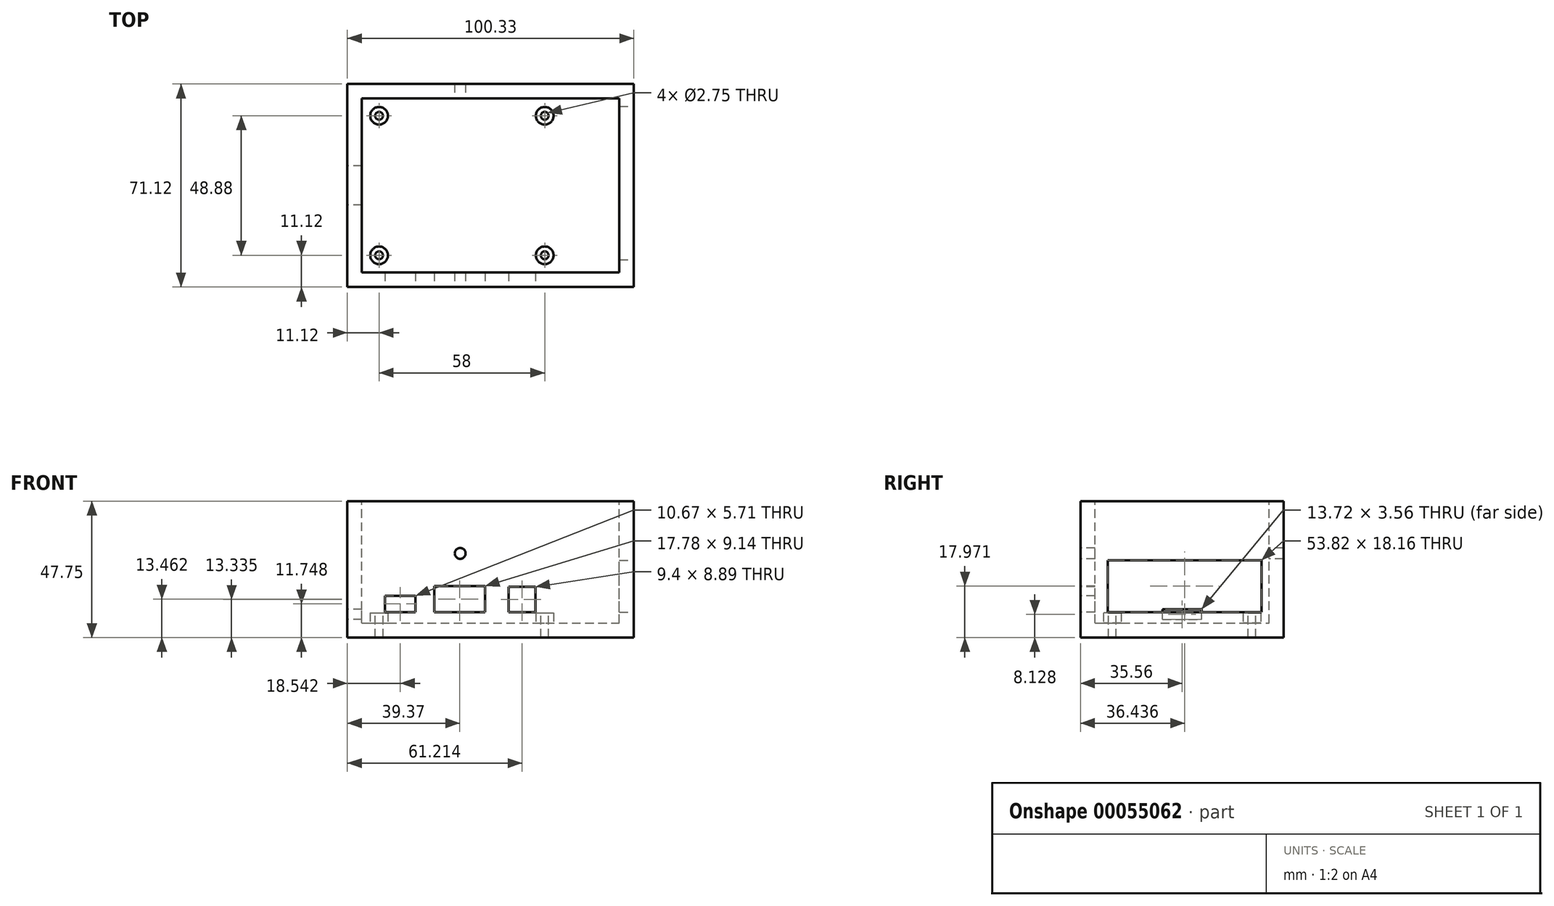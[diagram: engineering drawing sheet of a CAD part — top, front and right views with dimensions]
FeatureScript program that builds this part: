
annotation { "Feature Type Name" : "Feature", "Feature Type Description" : "" }
export const myFeature = defineFeature(function(context is Context, id is Id, definition is map)
    precondition{}
    {
        {
            var Q0;
            Q0=qCreatedBy(makeId("Top.planeOp"),FACE);
            var sketch = newSketch(context, id + "F0", { "sketchPlane" : qUnion([Q0])});
            skLineSegment(sketch, "E0.bottom", {"start": v(0, 0) * mm, "end": v(85.1, 0) * mm, "construction": true});
            skLineSegment(sketch, "E0.top", {"start": v(0, 55.88) * mm, "end": v(85.1, 55.88) * mm, "construction": true});
            skLineSegment(sketch, "E0.left", {"start": v(0, 0) * mm, "end": v(0, 55.88) * mm, "construction": true});
            skLineSegment(sketch, "E0.right", {"start": v(85.1, 0) * mm, "end": v(85.1, 55.88) * mm, "construction": true});
            skLineSegment(sketch, "E1", {"start": v(85.1, 54.61) * mm, "end": v(87.38, 54.61) * mm, "construction": true});
            skLineSegment(sketch, "E2", {"start": v(87.38, 54.61) * mm, "end": v(87.38, 2.29) * mm, "construction": true});
            skLineSegment(sketch, "E3", {"start": v(87.38, 2.29) * mm, "end": v(85.1, 2.29) * mm, "construction": true});
            skLineSegment(sketch, "E4", {"start": v(57.02, 0) * mm, "end": v(57.02, -2.29) * mm, "construction": true});
            skLineSegment(sketch, "E5", {"start": v(57.02, -2.29) * mm, "end": v(50.17, -2.29) * mm, "construction": true});
            skLineSegment(sketch, "E6", {"start": v(50.17, -2.29) * mm, "end": v(50.17, 0) * mm, "construction": true});
            skLineSegment(sketch, "E7", {"start": v(39.37, 0) * mm, "end": v(39.37, -0.76) * mm, "construction": true});
            skLineSegment(sketch, "E8", {"start": v(39.37, -0.76) * mm, "end": v(24.13, -0.76) * mm, "construction": true});
            skLineSegment(sketch, "E9", {"start": v(24.13, -0.76) * mm, "end": v(24.13, 0) * mm, "construction": true});
            skLineSegment(sketch, "E10", {"start": v(14.99, 0) * mm, "end": v(14.99, -1.27) * mm, "construction": true});
            skLineSegment(sketch, "E11", {"start": v(14.99, -1.27) * mm, "end": v(6.86, -1.27) * mm, "construction": true});
            skLineSegment(sketch, "E12", {"start": v(6.86, -1.27) * mm, "end": v(6.86, 0) * mm, "construction": true});
            skLineSegment(sketch, "E13", {"start": v(0, 33.53) * mm, "end": v(-2.54, 33.53) * mm, "construction": true});
            skLineSegment(sketch, "E14", {"start": v(-2.54, 33.53) * mm, "end": v(-2.54, 22.35) * mm, "construction": true});
            skLineSegment(sketch, "E15", {"start": v(-2.54, 22.35) * mm, "end": v(0, 22.35) * mm, "construction": true});
            skCircle(sketch, "E16", {"center": v(3.5, 52.38) * mm, "radius": 1.38 * mm});
            skCircle(sketch, "E17", {"center": v(3.5, 3.5) * mm, "radius": 1.38 * mm});
            skCircle(sketch, "E18", {"center": v(61.5, 3.5) * mm, "radius": 1.38 * mm});
            skCircle(sketch, "E19", {"center": v(61.5, 52.38) * mm, "radius": 1.38 * mm});
            skLineSegment(sketch, "E20.bottom", {"start": v(-2.54, -2.54) * mm, "end": v(87.63, -2.54) * mm});
            skLineSegment(sketch, "E20.top", {"start": v(-2.54, 58.42) * mm, "end": v(87.63, 58.42) * mm});
            skLineSegment(sketch, "E20.left", {"start": v(-2.54, -2.54) * mm, "end": v(-2.54, 58.42) * mm});
            skLineSegment(sketch, "E20.right", {"start": v(87.63, -2.54) * mm, "end": v(87.63, 58.42) * mm});
            skLineSegment(sketch, "E21.0", {"start": v(-7.62, -7.62) * mm, "end": v(92.71, -7.62) * mm});
            skLineSegment(sketch, "E21.1", {"start": v(-7.62, -7.62) * mm, "end": v(-7.62, 63.5) * mm});
            skLineSegment(sketch, "E21.2", {"start": v(-7.62, 63.5) * mm, "end": v(92.71, 63.5) * mm});
            skLineSegment(sketch, "E21.3", {"start": v(92.71, -7.62) * mm, "end": v(92.71, 63.5) * mm});
            skSolve(sketch);
        }
        {
            var Q0;
            Q0=makeQuery(id+"F0.imprint","IMPRINT",FACE,{"disambiguationData":[TD([[makeQuery(id+"F0.imprint","IMPRINT",EDGE,{"derivedFrom":sQuery(id+"F0.wireOp",EDGE,"E20.bottom")}),-1.0]])]});
            extrude(context, id + "F1", {"entities" : qUnion([Q0]), "oppositeDirection" : true, "depth" : 5.08 * mm});
        }
        {
            var Q0;
            Q0=makeQuery(id+"F1.opExtrude","CAP_FACE",FACE,{"disambiguationData":[OSD([sQuery(id+"F0.wireOp",EDGE,"E20.bottom"),sQuery(id+"F0.wireOp",EDGE,"E20.top"),sQuery(id+"F0.wireOp",EDGE,"E20.left"),sQuery(id+"F0.wireOp",EDGE,"E20.right"),sQuery(id+"F0.wireOp",EDGE,"E21.0"),sQuery(id+"F0.wireOp",EDGE,"E21.1"),sQuery(id+"F0.wireOp",EDGE,"E21.2"),sQuery(id+"F0.wireOp",EDGE,"E21.3")])],"isStart":false});
            var sketch = newSketch(context, id + "F2", { "sketchPlane" : qUnion([Q0])});
            skLineSegment(sketch, "E22.bottom", {"start": v(-7.62, 7.62) * mm, "end": v(92.71, 7.62) * mm});
            skLineSegment(sketch, "E22.top", {"start": v(-7.62, -63.5) * mm, "end": v(92.71, -63.5) * mm});
            skLineSegment(sketch, "E22.left", {"start": v(-7.62, 7.62) * mm, "end": v(-7.62, -63.5) * mm});
            skLineSegment(sketch, "E22.right", {"start": v(92.71, 7.62) * mm, "end": v(92.71, -63.5) * mm});
            skSolve(sketch);
        }
        {
            var Q0;
            Q0 = qSketchRegion(id + "F2", true);
            extrude(context, id + "F3", {"entities" : qUnion([Q0]), "operationType" : NewBodyOperationType.ADD, "depth" : 5.08 * mm});
        }
        {
            var Q0;
            Q0=makeQuery(id+"F0.imprint","IMPRINT",FACE,{"disambiguationData":[TD([[makeQuery(id+"F0.imprint","IMPRINT",EDGE,{"derivedFrom":sQuery(id+"F0.wireOp",EDGE,"E16")}),1.0]])]});
            var Q1;
            Q1=makeQuery(id+"F0.imprint","IMPRINT",FACE,{"disambiguationData":[TD([[makeQuery(id+"F0.imprint","IMPRINT",EDGE,{"derivedFrom":sQuery(id+"F0.wireOp",EDGE,"E19")}),1.0]])]});
            var Q2;
            Q2=makeQuery(id+"F0.imprint","IMPRINT",FACE,{"disambiguationData":[TD([[makeQuery(id+"F0.imprint","IMPRINT",EDGE,{"derivedFrom":sQuery(id+"F0.wireOp",EDGE,"E18")}),1.0]])]});
            var Q3;
            Q3=makeQuery(id+"F0.imprint","IMPRINT",FACE,{"disambiguationData":[TD([[makeQuery(id+"F0.imprint","IMPRINT",EDGE,{"derivedFrom":sQuery(id+"F0.wireOp",EDGE,"E17")}),1.0]])]});
            extrude(context, id + "F4", {"entities" : qUnion([Q0, Q1, Q2, Q3]), "operationType" : NewBodyOperationType.REMOVE, "oppositeDirection" : true, "depth" : 25.4 * mm});
        }
        {
            var Q0;
            Q0=makeQuery(id+"F3.opExtrude","CAP_FACE",FACE,{"disambiguationData":[OSD([sQuery(id+"F2.wireOp",EDGE,"E22.bottom"),sQuery(id+"F2.wireOp",EDGE,"E22.top"),sQuery(id+"F2.wireOp",EDGE,"E22.left"),sQuery(id+"F2.wireOp",EDGE,"E22.right")])],"isStart":true});
            var sketch = newSketch(context, id + "F5", { "sketchPlane" : qUnion([Q0])});
            skCircle(sketch, "E23", {"center": v(3.5, 52.38) * mm, "radius": 3.1 * mm});
            skCircle(sketch, "E24", {"center": v(61.5, 52.38) * mm, "radius": 3.1 * mm});
            skCircle(sketch, "E25", {"center": v(61.5, 3.5) * mm, "radius": 3.1 * mm});
            skCircle(sketch, "E26", {"center": v(3.5, 3.5) * mm, "radius": 3.1 * mm});
            skCircle(sketch, "E27", {"center": v(3.5, 52.38) * mm, "radius": 1.38 * mm});
            skCircle(sketch, "E28", {"center": v(3.5, 3.5) * mm, "radius": 1.38 * mm});
            skCircle(sketch, "E29", {"center": v(61.5, 3.5) * mm, "radius": 1.38 * mm});
            skCircle(sketch, "E30", {"center": v(61.5, 52.38) * mm, "radius": 1.38 * mm});
            skSolve(sketch);
        }
        {
            var Q0;
            Q0 = qSketchRegion(id + "F5", true);
            extrude(context, id + "F6", {"entities" : qUnion([Q0]), "operationType" : NewBodyOperationType.ADD, "depth" : 3.56 * mm});
        }
        {
            var Q0;
            Q0=makeQuery(id+"F0.imprint","IMPRINT",FACE,{"disambiguationData":[TD([[makeQuery(id+"F0.imprint","IMPRINT",EDGE,{"derivedFrom":sQuery(id+"F0.wireOp",EDGE,"E20.bottom")}),-1.0]])]});
            extrude(context, id + "F7", {"entities" : qUnion([Q0]), "operationType" : NewBodyOperationType.ADD, "depth" : 37.6 * mm});
        }
        {
            var Q0;
            {var subQ0=sQuery(id+"F0.wireOp",EDGE,"E21.1");Q0=makeQuery(id+"F7.boolean.opBoolean","MERGE",FACE,{"derivedFrom":[makeQuery(id+"F3.boolean.opBoolean","MERGE",FACE,{"derivedFrom":[makeQuery(id+"F1.opExtrude","SWEPT_FACE",FACE,{"disambiguationData":[OSD([subQ0])]}),makeQuery(id+"F3.opExtrude","SWEPT_FACE",FACE,{"disambiguationData":[OSD([sQuery(id+"F2.wireOp",EDGE,"E22.left")])]})]}),makeQuery(id+"F7.opExtrude","SWEPT_FACE",FACE,{"disambiguationData":[OSD([subQ0])]})]});}
            var sketch = newSketch(context, id + "F8", { "sketchPlane" : qUnion([Q0])});
            skLineSegment(sketch, "E31.rect.bottom", {"start": v(-21.08, -3.81) * mm, "end": v(-34.8, -3.81) * mm});
            skLineSegment(sketch, "E31.rect.top", {"start": v(-21.08, -0.25) * mm, "end": v(-34.8, -0.25) * mm});
            skLineSegment(sketch, "E31.rect.left", {"start": v(-21.08, -3.8) * mm, "end": v(-21.08, -0.25) * mm});
            skLineSegment(sketch, "E31.rect.right", {"start": v(-34.8, -3.81) * mm, "end": v(-34.8, -0.25) * mm});
            skPoint(sketch, "E31.rect.middle", {"position": v(-27.94, -2.03) * mm});
            skLineSegment(sketch, "E32.bottom", {"start": v(-33.53, -1.52) * mm, "end": v(-22.35, -1.52) * mm, "construction": true});
            skLineSegment(sketch, "E32.top", {"start": v(-33.53, -2.54) * mm, "end": v(-22.35, -2.54) * mm, "construction": true});
            skLineSegment(sketch, "E32.left", {"start": v(-33.53, -1.52) * mm, "end": v(-33.53, -2.54) * mm, "construction": true});
            skLineSegment(sketch, "E32.right", {"start": v(-22.35, -1.52) * mm, "end": v(-22.35, -2.54) * mm, "construction": true});
            skSolve(sketch);
        }
        {
            var Q0;
            Q0 = qSketchRegion(id + "F8", true);
            extrude(context, id + "F9", {"entities" : qUnion([Q0]), "operationType" : NewBodyOperationType.REMOVE, "endBound" : BoundingType.UP_TO_NEXT, "oppositeDirection" : true, "depth" : 25.4 * mm});
        }
        {
            var Q0;
            {var subQ0=sQuery(id+"F0.wireOp",EDGE,"E21.0");Q0=makeQuery(id+"F7.boolean.opBoolean","MERGE",FACE,{"derivedFrom":[makeQuery(id+"F3.boolean.opBoolean","MERGE",FACE,{"derivedFrom":[makeQuery(id+"F1.opExtrude","SWEPT_FACE",FACE,{"disambiguationData":[OSD([subQ0])]}),makeQuery(id+"F3.opExtrude","SWEPT_FACE",FACE,{"disambiguationData":[OSD([sQuery(id+"F2.wireOp",EDGE,"E22.bottom")])]})]}),makeQuery(id+"F7.opExtrude","SWEPT_FACE",FACE,{"disambiguationData":[OSD([subQ0])]})]});}
            var sketch = newSketch(context, id + "F10", { "sketchPlane" : qUnion([Q0])});
            skLineSegment(sketch, "E33.bottom", {"start": v(6.86, 3.18) * mm, "end": v(14.99, 3.18) * mm, "construction": true});
            skLineSegment(sketch, "E33.top", {"start": v(6.86, 0) * mm, "end": v(14.99, 0) * mm, "construction": true});
            skLineSegment(sketch, "E33.left", {"start": v(6.86, 3.18) * mm, "end": v(6.86, 0) * mm, "construction": true});
            skLineSegment(sketch, "E33.right", {"start": v(14.99, 3.18) * mm, "end": v(14.99, 0) * mm, "construction": true});
            skLineSegment(sketch, "E34.bottom", {"start": v(24.13, 6.6) * mm, "end": v(39.37, 6.6) * mm, "construction": true});
            skLineSegment(sketch, "E34.top", {"start": v(24.13, 0) * mm, "end": v(39.37, 0) * mm, "construction": true});
            skLineSegment(sketch, "E34.left", {"start": v(24.13, 6.6) * mm, "end": v(24.13, 0) * mm, "construction": true});
            skLineSegment(sketch, "E34.right", {"start": v(39.37, 6.6) * mm, "end": v(39.37, 0) * mm, "construction": true});
            skLineSegment(sketch, "E35.bottom", {"start": v(50.17, 6.35) * mm, "end": v(57.02, 6.35) * mm, "construction": true});
            skLineSegment(sketch, "E35.top", {"start": v(50.17, 0) * mm, "end": v(57.02, 0) * mm, "construction": true});
            skLineSegment(sketch, "E35.left", {"start": v(50.17, 6.35) * mm, "end": v(50.17, 0) * mm, "construction": true});
            skLineSegment(sketch, "E35.right", {"start": v(57.02, 6.35) * mm, "end": v(57.02, 0) * mm, "construction": true});
            skLineSegment(sketch, "E36.bottom", {"start": v(16.26, 4.45) * mm, "end": v(5.59, 4.45) * mm});
            skLineSegment(sketch, "E36.top", {"start": v(16.26, -1.27) * mm, "end": v(5.59, -1.27) * mm});
            skLineSegment(sketch, "E36.left", {"start": v(16.26, 4.45) * mm, "end": v(16.26, -1.27) * mm});
            skLineSegment(sketch, "E36.right", {"start": v(5.59, 4.45) * mm, "end": v(5.59, -1.27) * mm});
            skLineSegment(sketch, "E37.bottom", {"start": v(22.86, 7.87) * mm, "end": v(40.64, 7.87) * mm});
            skLineSegment(sketch, "E37.top", {"start": v(22.86, -1.27) * mm, "end": v(40.64, -1.27) * mm});
            skLineSegment(sketch, "E37.left", {"start": v(22.86, 7.87) * mm, "end": v(22.86, -1.27) * mm});
            skLineSegment(sketch, "E37.right", {"start": v(40.64, 7.87) * mm, "end": v(40.64, -1.27) * mm});
            skLineSegment(sketch, "E38.bottom", {"start": v(48.9, 7.62) * mm, "end": v(58.3, 7.62) * mm});
            skLineSegment(sketch, "E38.top", {"start": v(48.9, -1.27) * mm, "end": v(58.3, -1.27) * mm});
            skLineSegment(sketch, "E38.left", {"start": v(48.9, 7.62) * mm, "end": v(48.9, -1.27) * mm});
            skLineSegment(sketch, "E38.right", {"start": v(58.3, 7.62) * mm, "end": v(58.3, -1.27) * mm});
            skPoint(sketch, "E39", {"position": v(14.99, 1.59) * mm});
            skPoint(sketch, "E40", {"position": v(10.92, 0) * mm});
            skPoint(sketch, "E41", {"position": v(10.92, -1.27) * mm});
            skPoint(sketch, "E42", {"position": v(16.26, 1.59) * mm});
            skPoint(sketch, "E43", {"position": v(22.86, 3.3) * mm});
            skPoint(sketch, "E44", {"position": v(31.75, -1.27) * mm});
            skPoint(sketch, "E45", {"position": v(31.75, 0) * mm});
            skPoint(sketch, "E46", {"position": v(24.13, 3.3) * mm});
            skPoint(sketch, "E47", {"position": v(58.3, 3.18) * mm});
            skPoint(sketch, "E48", {"position": v(53.6, -1.27) * mm});
            skPoint(sketch, "E49", {"position": v(53.6, 0) * mm});
            skPoint(sketch, "E50", {"position": v(57.02, 3.18) * mm});
            skLineSegment(sketch, "E51", {"start": v(14.99, 0) * mm, "end": v(14.99, -1.27) * mm, "construction": true});
            skLineSegment(sketch, "E52", {"start": v(14.99, 0) * mm, "end": v(16.26, 0) * mm, "construction": true});
            skLineSegment(sketch, "E53", {"start": v(24.13, 0) * mm, "end": v(22.86, 0) * mm, "construction": true});
            skLineSegment(sketch, "E54", {"start": v(24.13, 0) * mm, "end": v(24.13, -1.27) * mm, "construction": true});
            skLineSegment(sketch, "E55", {"start": v(50.17, 0) * mm, "end": v(48.9, 0) * mm, "construction": true});
            skLineSegment(sketch, "E56", {"start": v(50.17, 0) * mm, "end": v(50.17, -1.27) * mm, "construction": true});
            skSolve(sketch);
        }
        {
            var Q0;
            Q0 = qSketchRegion(id + "F10", true);
            extrude(context, id + "F11", {"entities" : qUnion([Q0]), "operationType" : NewBodyOperationType.REMOVE, "endBound" : BoundingType.UP_TO_NEXT, "oppositeDirection" : true, "depth" : 25.4 * mm});
        }
        {
            var Q0;
            {var subQ0=sQuery(id+"F0.wireOp",EDGE,"E21.3");Q0=makeQuery(id+"F7.boolean.opBoolean","MERGE",FACE,{"derivedFrom":[makeQuery(id+"F3.boolean.opBoolean","MERGE",FACE,{"derivedFrom":[makeQuery(id+"F1.opExtrude","SWEPT_FACE",FACE,{"disambiguationData":[OSD([subQ0])]}),makeQuery(id+"F3.opExtrude","SWEPT_FACE",FACE,{"disambiguationData":[OSD([sQuery(id+"F2.wireOp",EDGE,"E22.right")])]})]}),makeQuery(id+"F7.opExtrude","SWEPT_FACE",FACE,{"disambiguationData":[OSD([subQ0])]})]});}
            var sketch = newSketch(context, id + "F12", { "sketchPlane" : qUnion([Q0])});
            skLineSegment(sketch, "E57.bottom", {"start": v(2.54, 13.72) * mm, "end": v(18.54, 13.72) * mm, "construction": true});
            skLineSegment(sketch, "E57.top", {"start": v(2.54, 0) * mm, "end": v(18.54, 0) * mm, "construction": true});
            skLineSegment(sketch, "E57.left", {"start": v(2.54, 13.72) * mm, "end": v(2.54, 0) * mm, "construction": true});
            skLineSegment(sketch, "E57.right", {"start": v(18.54, 13.72) * mm, "end": v(18.54, 0) * mm, "construction": true});
            skLineSegment(sketch, "E58.bottom", {"start": v(21.44, 16.26) * mm, "end": v(36.68, 16.26) * mm, "construction": true});
            skLineSegment(sketch, "E58.top", {"start": v(21.44, 0) * mm, "end": v(36.68, 0) * mm, "construction": true});
            skLineSegment(sketch, "E58.left", {"start": v(21.44, 16.26) * mm, "end": v(21.44, 0) * mm, "construction": true});
            skLineSegment(sketch, "E58.right", {"start": v(36.68, 16.26) * mm, "end": v(36.68, 0) * mm, "construction": true});
            skLineSegment(sketch, "E59.bottom", {"start": v(39.22, 16.26) * mm, "end": v(54.46, 16.26) * mm, "construction": true});
            skLineSegment(sketch, "E59.top", {"start": v(39.22, 0) * mm, "end": v(54.46, 0) * mm, "construction": true});
            skLineSegment(sketch, "E59.left", {"start": v(39.22, 16.26) * mm, "end": v(39.22, 0) * mm, "construction": true});
            skLineSegment(sketch, "E59.right", {"start": v(54.46, 16.26) * mm, "end": v(54.46, 0) * mm, "construction": true});
            skLineSegment(sketch, "E60.bottom", {"start": v(1.9, 16.9) * mm, "end": v(55.73, 16.9) * mm});
            skLineSegment(sketch, "E60.top", {"start": v(1.9, -1.27) * mm, "end": v(55.73, -1.27) * mm});
            skLineSegment(sketch, "E60.left", {"start": v(1.9, 16.9) * mm, "end": v(1.9, -1.27) * mm});
            skLineSegment(sketch, "E60.right", {"start": v(55.73, 16.9) * mm, "end": v(55.73, -1.27) * mm});
            skSolve(sketch);
        }
        {
            var Q0;
            Q0 = qSketchRegion(id + "F12", true);
            extrude(context, id + "F13", {"entities" : qUnion([Q0]), "operationType" : NewBodyOperationType.REMOVE, "endBound" : BoundingType.UP_TO_NEXT, "oppositeDirection" : true, "depth" : 25.4 * mm});
        }
        {
            var Q0;
            {var subQ0=sQuery(id+"F0.wireOp",EDGE,"E21.0");Q0=makeQuery(id+"F7.boolean.opBoolean","MERGE",FACE,{"derivedFrom":[makeQuery(id+"F3.boolean.opBoolean","MERGE",FACE,{"derivedFrom":[makeQuery(id+"F1.opExtrude","SWEPT_FACE",FACE,{"disambiguationData":[OSD([subQ0])]}),makeQuery(id+"F3.opExtrude","SWEPT_FACE",FACE,{"disambiguationData":[OSD([sQuery(id+"F2.wireOp",EDGE,"E22.bottom")])]})]}),makeQuery(id+"F7.opExtrude","SWEPT_FACE",FACE,{"disambiguationData":[OSD([subQ0])]})]});}
            var sketch = newSketch(context, id + "F14", { "sketchPlane" : qUnion([Q0])});
            skCircle(sketch, "E61", {"center": v(31.9, 19.3) * mm, "radius": 1.9 * mm});
            skSolve(sketch);
        }
        {
            var Q0;
            Q0 = qSketchRegion(id + "F14", true);
            extrude(context, id + "F15", {"entities" : qUnion([Q0]), "operationType" : NewBodyOperationType.REMOVE, "endBound" : BoundingType.THROUGH_ALL, "oppositeDirection" : true, "depth" : 25.4 * mm});
        }
    });
